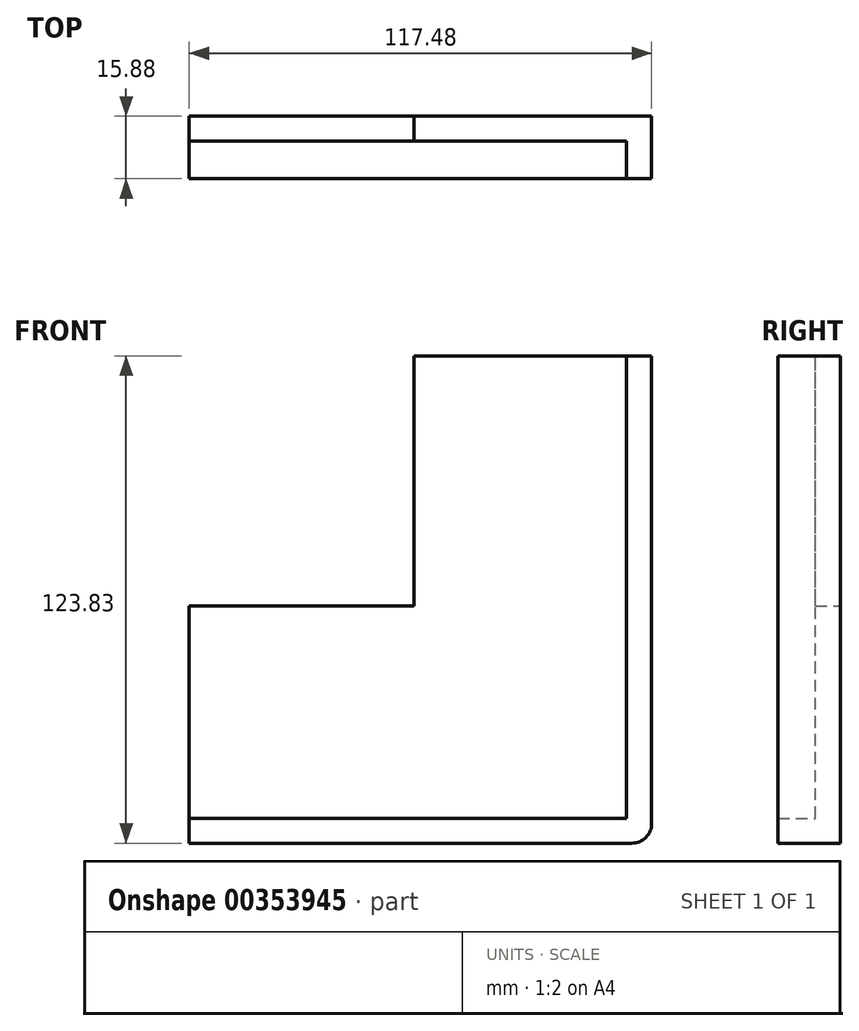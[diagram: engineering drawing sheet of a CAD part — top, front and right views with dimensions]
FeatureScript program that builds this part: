
annotation { "Feature Type Name" : "Feature", "Feature Type Description" : "" }
export const myFeature = defineFeature(function(context is Context, id is Id, definition is map)
    precondition{}
    {
        {
            var Q0;
            Q0=qCreatedBy(makeId("Front.planeOp"),FACE);
            var sketch = newSketch(context, id + "F0", { "sketchPlane" : qUnion([Q0])});
            skLineSegment(sketch, "E0", {"start": v(0, 0) * mm, "end": v(0, 63.5) * mm});
            skLineSegment(sketch, "E1", {"start": v(0, 63.5) * mm, "end": v(60.33, 63.5) * mm});
            skLineSegment(sketch, "E2", {"start": v(60.33, 63.5) * mm, "end": v(60.33, -60.32) * mm});
            skLineSegment(sketch, "E3", {"start": v(60.33, -60.32) * mm, "end": v(-57.15, -60.33) * mm});
            skLineSegment(sketch, "E4", {"start": v(-57.15, -60.33) * mm, "end": v(-57.15, 0) * mm});
            skLineSegment(sketch, "E5", {"start": v(-57.15, 0) * mm, "end": v(0, 0) * mm});
            skSolve(sketch);
        }
        {
            var Q0;
            Q0=makeQuery(id+"F0.imprint","IMPRINT",FACE,{"disambiguationData":[TD([[makeQuery(id+"F0.imprint","IMPRINT",EDGE,{"derivedFrom":sQuery(id+"F0.wireOp",EDGE,"E0")}),-1.0]])]});
            extrude(context, id + "F1", {"entities" : qUnion([Q0]), "depth" : 6.35 * mm});
        }
        {
            var Q0;
            Q0=makeQuery(id+"F1.opExtrude","CAP_FACE",FACE,{"disambiguationData":[OSD([sQuery(id+"F0.wireOp",EDGE,"E0"),sQuery(id+"F0.wireOp",EDGE,"E1"),sQuery(id+"F0.wireOp",EDGE,"E2"),sQuery(id+"F0.wireOp",EDGE,"E3"),sQuery(id+"F0.wireOp",EDGE,"E4"),sQuery(id+"F0.wireOp",EDGE,"E5")])],"isStart":false});
            var sketch = newSketch(context, id + "F2", { "sketchPlane" : qUnion([Q0])});
            skLineSegment(sketch, "E6", {"start": v(-57.15, -60.33) * mm, "end": v(-57.15, -53.97) * mm});
            skLineSegment(sketch, "E7", {"start": v(-57.15, -53.97) * mm, "end": v(53.98, -53.97) * mm});
            skLineSegment(sketch, "E8", {"start": v(53.98, -53.98) * mm, "end": v(53.98, 63.5) * mm});
            skLineSegment(sketch, "E9", {"start": v(53.98, 63.5) * mm, "end": v(60.33, 63.5) * mm});
            skLineSegment(sketch, "E10", {"start": v(60.33, 63.5) * mm, "end": v(60.33, -60.32) * mm});
            skLineSegment(sketch, "E11", {"start": v(60.33, -60.32) * mm, "end": v(-57.15, -60.33) * mm});
            skSolve(sketch);
        }
        {
            var Q0;
            Q0=makeQuery(id+"F2.imprint","IMPRINT",FACE,{"disambiguationData":[TD([[makeQuery(id+"F2.imprint","IMPRINT",EDGE,{"derivedFrom":sQuery(id+"F2.wireOp",EDGE,"E6")}),-1.0]])]});
            extrude(context, id + "F3", {"entities" : qUnion([Q0]), "operationType" : NewBodyOperationType.ADD, "depth" : 9.52 * mm});
        }
        {
            var Q0;
            Q0=makeQuery(id+"F3.boolean.opBoolean","MERGE",EDGE,{"derivedFrom":[makeQuery(id+"F1.opExtrude","SWEPT_EDGE",EDGE,{"disambiguationData":[OSD([sQuery(id+"F0.wireOp",EDGE,"E2"),sQuery(id+"F0.wireOp",EDGE,"E3")])]}),makeQuery(id+"F3.opExtrude","SWEPT_EDGE",EDGE,{"disambiguationData":[OSD([sQuery(id+"F2.wireOp",EDGE,"E10"),sQuery(id+"F2.wireOp",EDGE,"E11")])]})]});
            fillet(context, id + "F4", {"entities" : qUnion([Q0]), "radius" : 5.08 * mm, "tangentPropagation" : true, "allowEdgeOverflow" : false});
        }
    });
